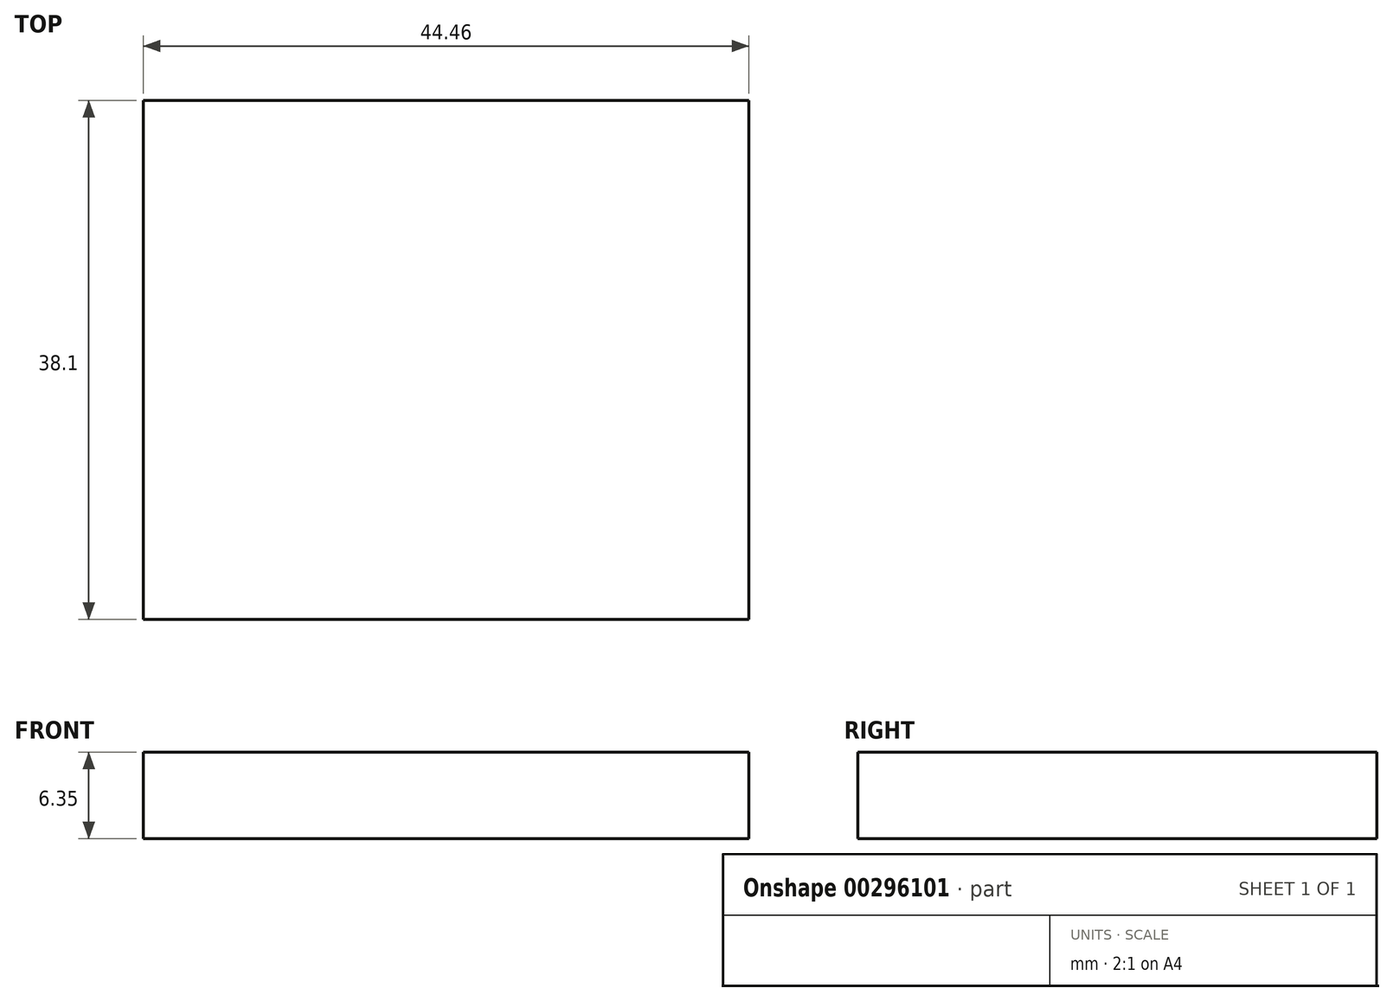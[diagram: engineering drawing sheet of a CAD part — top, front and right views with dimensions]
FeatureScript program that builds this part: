
annotation { "Feature Type Name" : "Feature", "Feature Type Description" : "" }
export const myFeature = defineFeature(function(context is Context, id is Id, definition is map)
    precondition{}
    {
        {
            var Q0;
            Q0=qCreatedBy(makeId("Top.planeOp"),FACE);
            var sketch = newSketch(context, id + "F0", { "sketchPlane" : qUnion([Q0])});
            skLineSegment(sketch, "E0.bottom", {"start": v(22.22, 19.05) * mm, "end": v(-22.23, 19.05) * mm});
            skLineSegment(sketch, "E0.top", {"start": v(22.23, -19.05) * mm, "end": v(-22.22, -19.05) * mm});
            skLineSegment(sketch, "E0.left", {"start": v(22.22, 19.05) * mm, "end": v(22.23, -19.05) * mm});
            skLineSegment(sketch, "E0.right", {"start": v(-22.23, 19.05) * mm, "end": v(-22.22, -19.05) * mm});
            skPoint(sketch, "E0.middle", {"position": v(0, 0) * mm});
            skSolve(sketch);
        }
        {
            var Q0;
            Q0=makeQuery(id+"F0.imprint","IMPRINT",FACE,{"disambiguationData":[TD([[makeQuery(id+"F0.imprint","IMPRINT",EDGE,{"derivedFrom":sQuery(id+"F0.wireOp",EDGE,"E0.bottom")}),1.0]])]});
            extrude(context, id + "F1", {"entities" : qUnion([Q0]), "depth" : 6.35 * mm});
        }
    });
